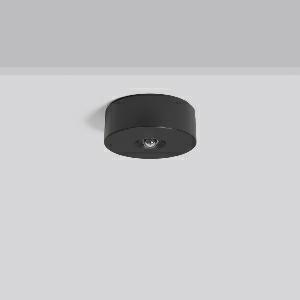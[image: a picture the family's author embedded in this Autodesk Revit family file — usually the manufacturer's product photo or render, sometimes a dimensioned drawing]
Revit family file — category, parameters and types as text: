
# Revit family: lucio_2_672529_003_89_ff26
name_source: partatom
category: Lighting Fixtures
units: mm (PartAtom-declared; Revit-internal decimal feet)

## family parameters
Cut with Voids When Loaded = No
Host = Face
Light Source = No
Part Type = Normal
Room Calculation Point = No
Round Connector Dimension = Use Diameter
Shared = No

## types (1)
- Flaechenlinse (1 x LED Modul 740, 310 lm, 4000)
    Apparent Load = 5 VA
    CIE Flux Codes = 44 87 99 100 100
    Color Rendering = 70
    Color Temperature = 4000
    Default Elevation = 1800 mm
    Description = Series: LUCIO 2
Round surface-mounted downlight. For escape route illumination. Housing: plastic (polycarbonate). Cover: polycarbonate. Plastic lenses for area lighting and escape route illumination included in scope of delivery. Suitable for Ceiling mounting. Driver integrated. Suitable for connection to central battery systems. With AC Control monitoring module for LUXIFAIR central battery units. 
Colour: black
Diameter: 110 mm
Height: 46 mm
Weight: 0.19 kg
Operating mode: non-maintained power mode
Lamp: LED
Socket: without socket
Colour temperature: 4000K
Colour rendering index (CRI): 70
Luminous flux, emergency: 310 lm
System power, emergency: 5.6 W
Luminous flux, emergency 2: 290 lm
System power, emergency 2: 5.6 W
Control gear: EB
Protection class: II
Type of protection: IP 20
    Height = 46 mm
    Lamp = 1 x LED Modul 740
    Lamp Light Flux = 310 lm
    Lamp count = 1
    Length = 110 mm
    Lifetime = 50000 h
    Luminous efficacy = 60 lm/W
    Manufacturer = RZB
    ModVariant = No
    Model = 672529.003.89
    Mounting Place = Ceiling
    Mounting Type = Surface mounted
    Number of Poles = 1
    OnlyDefault = Yes
    Power Factor = 1
    Product Name = LUCIO 2
    Product group = Surface mounted ceiling luminaires
    ProductGroupID = 303
    Protection Class = Protection class II
    Protection Degree = Degree of protection
    RLX_Detail_Level = 1
    RLX_Emergency_Light_Flux = 310 lm
    RLX_Emergency_Type = 3
    RLX_Emergency_Type_DB = Yes
    RlxData = <blob elided: 167709 chars, md5=67e0d2cd>
    Socket = socket
    Standby Power = 0 W
    System Light Flux = 310 lm
    System Power = 5 W
    Type Comments = Area lens
    Type Image = 672527.003.jpg
    URL = http://relux.com
    VarID = flaechenlinse
    Voltage = 0 V
    Weight = 0.00 kg
    Width = 0 mm  [stored 0 ft]

note: [stored X ft] marks values corroborated as IEEE doubles in the binary element streams (Revit-internal decimal feet)

## geometry (parser evidence)
native form markers: Blend x4, Sweep x10
no freeform markers — native parametric forms only
